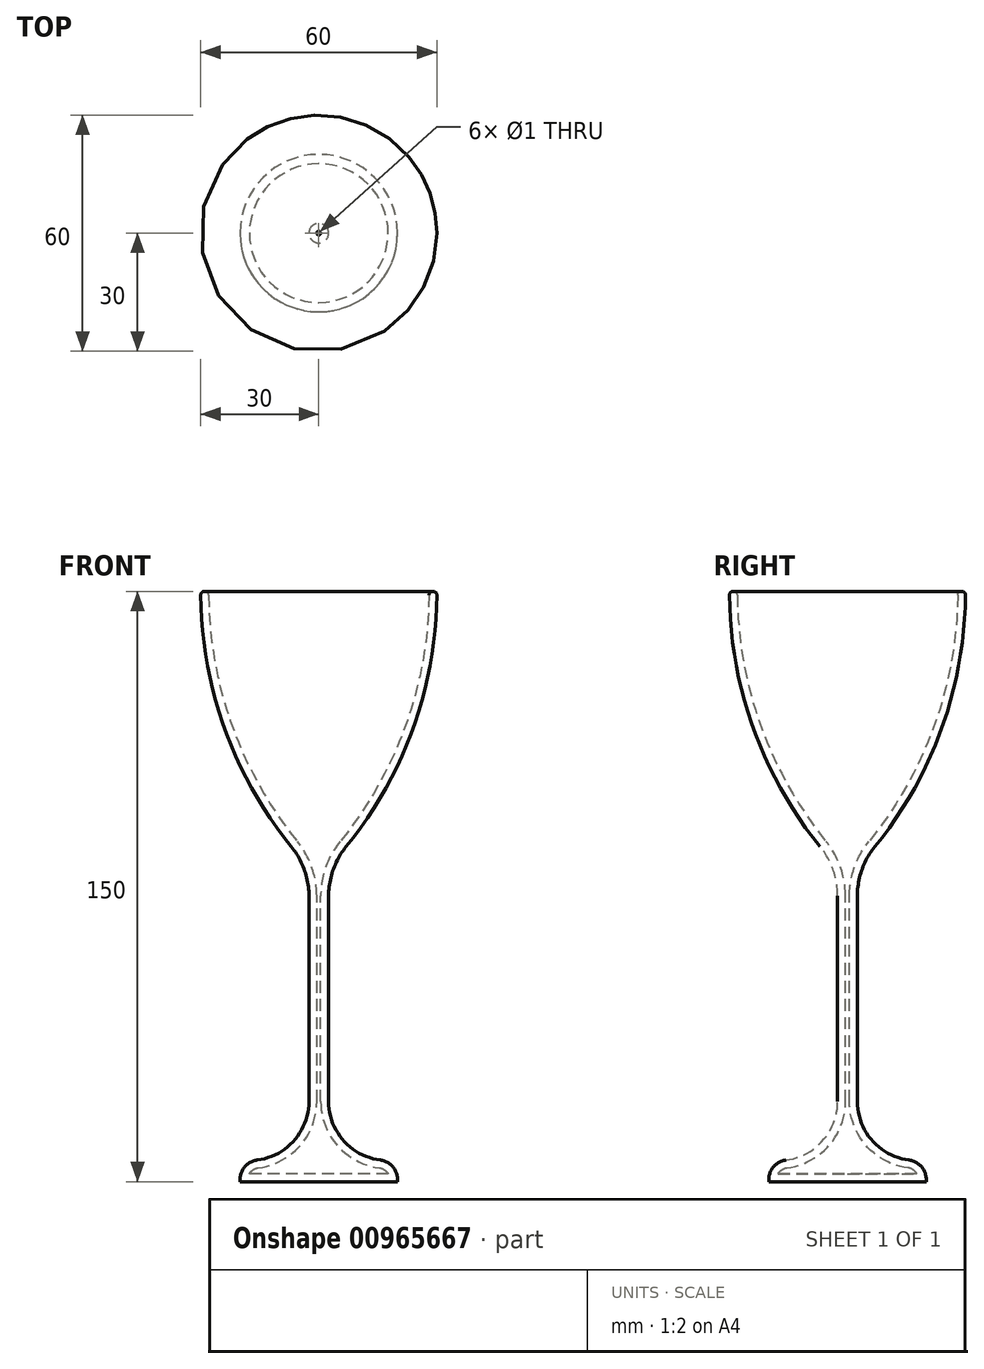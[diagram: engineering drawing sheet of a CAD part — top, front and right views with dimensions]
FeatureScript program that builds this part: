
annotation { "Feature Type Name" : "Feature", "Feature Type Description" : "" }
export const myFeature = defineFeature(function(context is Context, id is Id, definition is map)
    precondition{}
    {
        {
            var Q0;
            Q0=qCreatedBy(makeId("Front.planeOp"),FACE);
            var sketch = newSketch(context, id + "F0", { "sketchPlane" : qUnion([Q0])});
            skLineSegment(sketch, "E0", {"start": v(0, 150) * mm, "end": v(0, 0) * mm});
            skLineSegment(sketch, "E1", {"start": v(0, 0) * mm, "end": v(20, 0) * mm});
            skLineSegment(sketch, "E2", {"start": v(20, 0) * mm, "end": v(20, 5) * mm});
            skLineSegment(sketch, "E3", {"start": v(20, 5) * mm, "end": v(2.5, 7) * mm});
            skLineSegment(sketch, "E4", {"start": v(2.5, 7) * mm, "end": v(2.5, 80) * mm});
            skArc(sketch, "E5", {"start": v(2.5, 80) * mm, "mid": v(22.88, 112.4) * mm, "end": v(30, 150) * mm});
            skLineSegment(sketch, "E6", {"start": v(30, 150) * mm, "end": v(0, 150) * mm});
            skLineSegment(sketch, "E7", {"start": v(30, 150) * mm, "end": v(30, 92.25) * mm, "construction": true});
            skSolve(sketch);
        }
        {
            var Q0;
            Q0 = qSketchRegion(id + "F0", true);
            var Q1;
            Q1=sQuery(id+"F0.wireOp",EDGE,"E0");
            revolve(context, id + "F1", {"surfaceOperationType" : NewSurfaceOperationType.NEW, "entities" : qUnion([Q0]), "axis" : qUnion([Q1]), "revolveType" : RevolveType.FULL});
        }
        {
            var Q0;
            Q0=makeQuery(id+"F1.opRevolve","SWEPT_EDGE",EDGE,{"disambiguationData":[OSD([sQuery(id+"F0.wireOp",EDGE,"E3"),sQuery(id+"F0.wireOp",EDGE,"E4")])]});
            fillet(context, id + "F2", {"entities" : qUnion([Q0]), "radius" : 15 * mm, "tangentPropagation" : true, "allowEdgeOverflow" : false});
        }
        {
            var Q0;
            Q0=makeQuery(id+"F1.opRevolve","SWEPT_EDGE",EDGE,{"disambiguationData":[OSD([sQuery(id+"F0.wireOp",EDGE,"E2"),sQuery(id+"F0.wireOp",EDGE,"E3")])]});
            fillet(context, id + "F3", {"entities" : qUnion([Q0]), "radius" : 5 * mm, "tangentPropagation" : true, "allowEdgeOverflow" : false});
        }
        {
            var Q0;
            Q0=makeQuery(id+"F1.opRevolve","SWEPT_EDGE",EDGE,{"disambiguationData":[OSD([sQuery(id+"F0.wireOp",EDGE,"E4"),sQuery(id+"F0.wireOp",EDGE,"E5")])]});
            fillet(context, id + "F4", {"entities" : qUnion([Q0]), "radius" : 20 * mm, "tangentPropagation" : true, "allowEdgeOverflow" : false});
        }
        {
            var Q0;
            Q0=makeQuery(id+"F1.opRevolve","SWEPT_FACE",FACE,{"disambiguationData":[OSD([sQuery(id+"F0.wireOp",EDGE,"E6")])]});
            shell(context, id + "F5", {"entities" : qUnion([Q0]), "thickness" : 2 * mm});
        }
        {
            var Q0;
            Q0=makeQuery(id+"F1.opRevolve","SWEPT_EDGE",EDGE,{"disambiguationData":[OSD([sQuery(id+"F0.wireOp",EDGE,"E5"),sQuery(id+"F0.wireOp",EDGE,"E6")])]});
            var Q1;
            Q1=makeQuery(id+"F5.opShell","OFFSET_EDGE",EDGE,{"disambiguationData":[OSD([sQuery(id+"F0.wireOp",EDGE,"E5"),sQuery(id+"F0.wireOp",EDGE,"E6")])]});
            fillet(context, id + "F6", {"entities" : qUnion([Q0, Q1]), "radius" : 1 * mm, "tangentPropagation" : true, "allowEdgeOverflow" : false});
        }
    });
